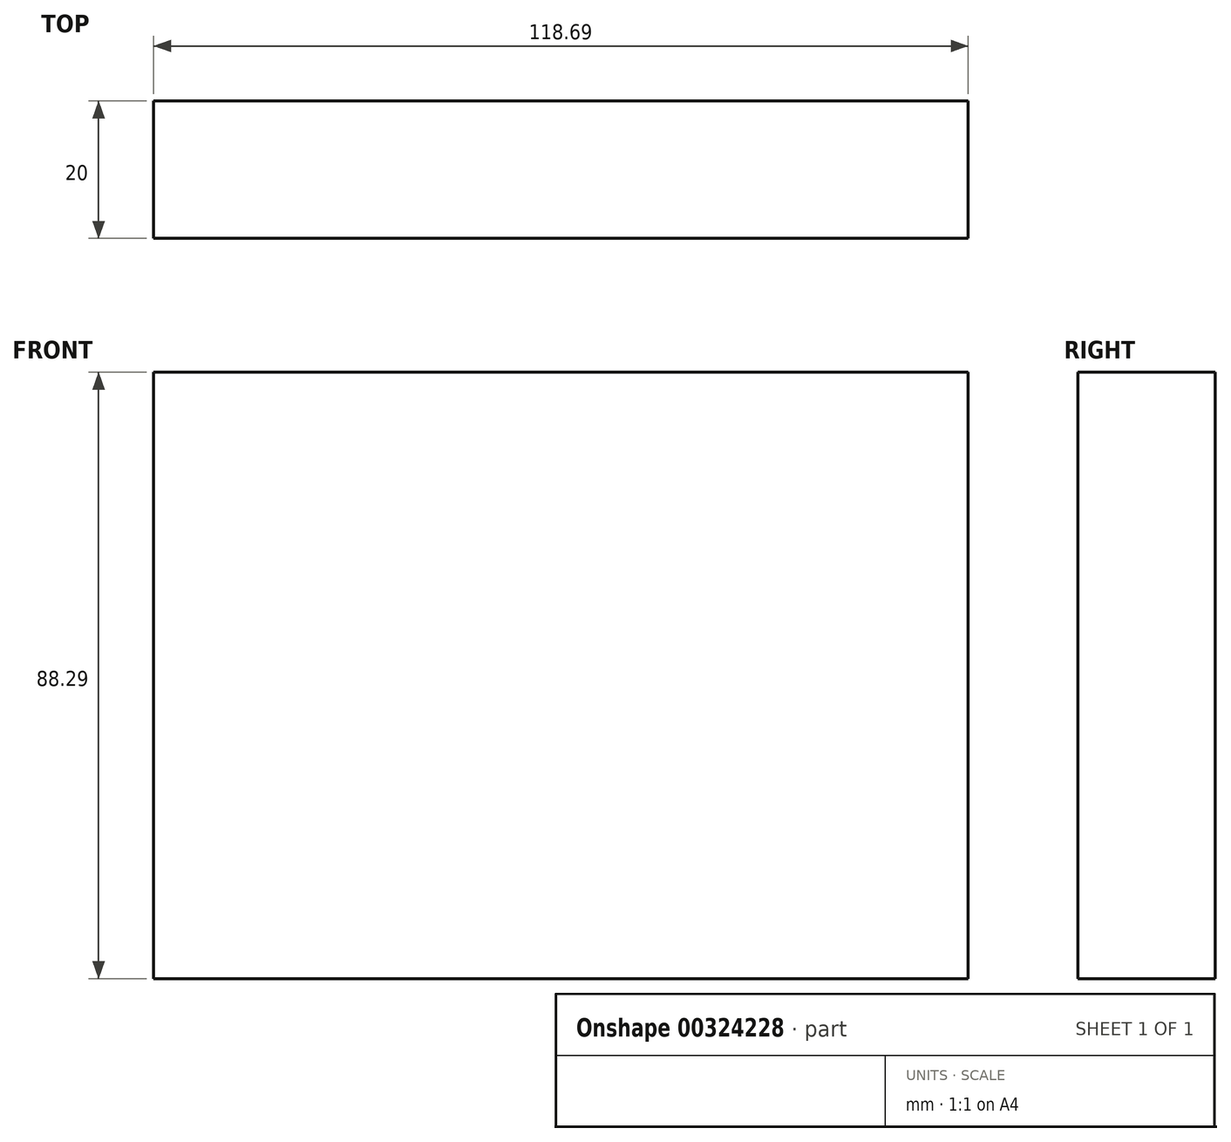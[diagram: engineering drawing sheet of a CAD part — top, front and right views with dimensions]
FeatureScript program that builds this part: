
annotation { "Feature Type Name" : "Feature", "Feature Type Description" : "" }
export const myFeature = defineFeature(function(context is Context, id is Id, definition is map)
    precondition{}
    {
        {
            var Q0;
            Q0=qCreatedBy(makeId("Front.planeOp"),FACE);
            var sketch = newSketch(context, id + "F0", { "sketchPlane" : qUnion([Q0])});
            skLineSegment(sketch, "E0.bottom", {"start": v(-53.27, 51.89) * mm, "end": v(65.42, 51.89) * mm});
            skLineSegment(sketch, "E0.top", {"start": v(-53.27, -36.4) * mm, "end": v(65.42, -36.4) * mm});
            skLineSegment(sketch, "E0.left", {"start": v(-53.27, 51.89) * mm, "end": v(-53.27, -36.4) * mm});
            skLineSegment(sketch, "E0.right", {"start": v(65.42, 51.89) * mm, "end": v(65.42, -36.4) * mm});
            skSolve(sketch);
        }
        {
            var Q0;
            Q0=makeQuery(id+"F0.imprint","IMPRINT",FACE,{"disambiguationData":[TD([[makeQuery(id+"F0.imprint","IMPRINT",EDGE,{"derivedFrom":sQuery(id+"F0.wireOp",EDGE,"E0.bottom")}),-1.0]])]});
            extrude(context, id + "F1", {"entities" : qUnion([Q0]), "depth" : 20 * mm});
        }
    });
